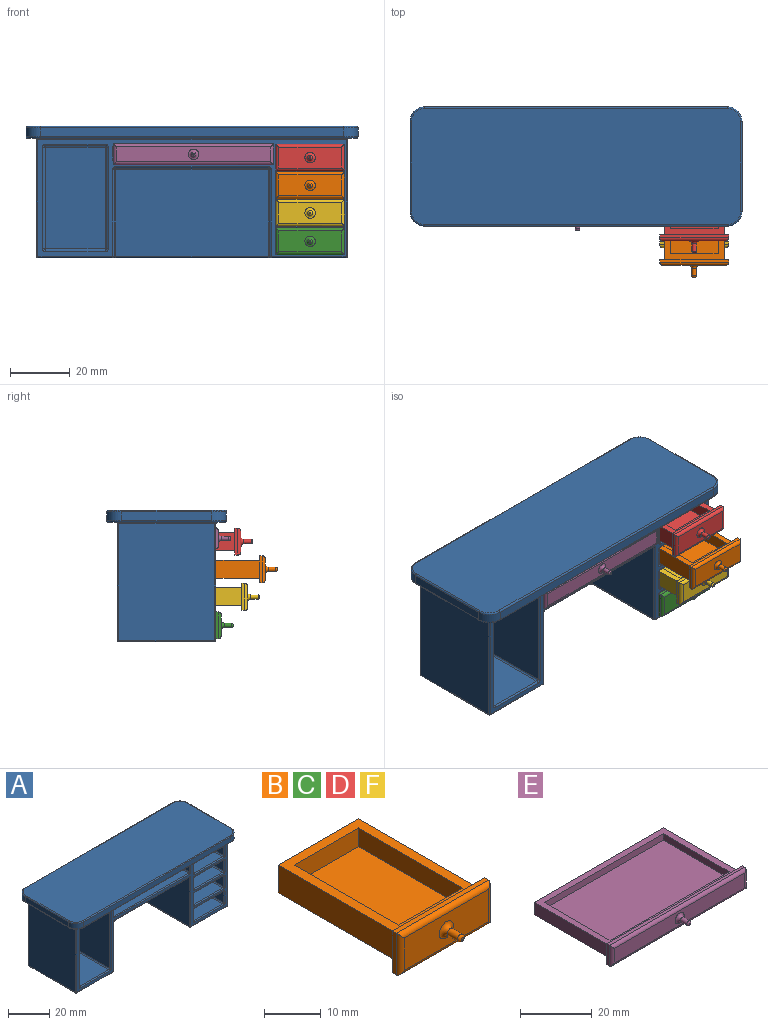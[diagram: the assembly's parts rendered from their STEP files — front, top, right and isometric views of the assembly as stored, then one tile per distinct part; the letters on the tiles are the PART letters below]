
ASSEMBLY  parts=6 mates=10
PART A: 225 faces, bbox 111.9x40.8x44 mm
  f0: plane 110.03x39mm, normal (0,0,-1), area 703.6mm2, adj f169,f170,f171,f173,f174,f175,f179,f180
  f1: plane 103.03x39mm, normal (0,-1,0), area 596.7mm2, adj f49,f50,f51,f52,f56,f57,f58,f61
  f2: plane 29x6.5mm, normal (-1,0,0), area 188.5mm2, adj f69,f72,f76,f77
  f3: plane 29x6.5mm, normal (1,0,0), area 188.5mm2, adj f74,f83,f84,f88
  f4: plane 20x6.25mm, normal (0,-1,0), area 125mm2, adj f54,f63,f64,f68
  f5: plane 29x6.25mm, normal (-1,0,0), area 181.2mm2, adj f57,f62,f65,f68
  f6: plane 29x6.25mm, normal (1,0,0), area 181.2mm2, adj f49,f53,f54,f55
  f7: plane 20x6.25mm, normal (0,-1,0), area 125mm2, adj f94,f103,f104,f108
  f8: plane 20x6mm, normal (0,-1,0), area 120mm2, adj f114,f123,f124,f128
  f9: plane 29x6.25mm, normal (-1,0,0), area 181.2mm2, adj f97,f102,f105,f108
  f10: plane 29x6.25mm, normal (1,0,0), area 181.2mm2, adj f89,f93,f94,f95
  f11: plane 29x29mm, normal (1,0,0), area 841mm2, adj f192,f193,f202,f203
  f12: plane 29x29mm, normal (-1,0,0), area 841mm2, adj f195,f196,f204,f205
  f13: plane 51.03x29mm, normal (0,0,-1), area 1479.8mm2, adj f184,f193,f194,f195
  f14: plane 30x3mm, normal (1,0,0), area 90mm2, adj f15,f21,f213,f221
  f15: cylinder r=5mm len=5mm, axis (0,0,1), area 23.6mm2, adj f14,f16,f211,f219
  f16: plane 101.03x3mm, normal (0,1,0), area 303.1mm2, adj f15,f17,f209,f217
  f17: cylinder r=5mm len=5mm, axis (0,0,1), area 23.6mm2, adj f16,f18,f210,f218
  f18: plane 30x3mm, normal (-1,0,0), area 90mm2, adj f17,f19,f212,f220
  f19: cylinder r=5mm len=5mm, axis (0,0,1), area 23.6mm2, adj f18,f20,f214,f222
  f20: plane 101.03x3mm, normal (0,-1,0), area 303.1mm2, adj f19,f21,f216,f224
  f21: cylinder r=5mm len=5mm, axis (0,0,1), area 23.6mm2, adj f14,f20,f215,f223
  f22: plane 110.03x39mm, normal (0,0,1), area 4273.7mm2, adj f209,f210,f211,f212,f213,f214,f215,f216
  f23: plane 39x32mm, normal (-1,0,0), area 1248mm2, adj f172,f173,f182,f183
  f24: plane 103.03x39mm, normal (0,1,0), area 4018.1mm2, adj f169,f172,f176,f177
  f25: plane 103.03x32mm, normal (0,0,-1), area 1706.5mm2, adj f177,f182,f186,f191,f197,f202,f205,f206
  f26: plane 39x32mm, normal (1,0,0), area 1248mm2, adj f175,f176,f185,f186
  f27: plane 51.03x29mm, normal (0,-1,0), area 1479.8mm2, adj f194,f203,f204,f208
  f28: plane 51.03x4mm, normal (0,-1,0), area 204.1mm2, adj f137,f142,f145,f148
  f29: plane 29x4mm, normal (1,0,0), area 116mm2, adj f135,f136,f144,f145
  f30: plane 51.03x29mm, normal (0,0,-1), area 1479.8mm2, adj f129,f132,f136,f137
  f31: plane 51.03x29mm, normal (0,0,1), area 1479.8mm2, adj f134,f143,f144,f148
  f32: plane 29x4mm, normal (-1,0,0), area 116mm2, adj f132,f133,f142,f143
  f33: plane 20x6.5mm, normal (0,-1,0), area 130mm2, adj f69,f73,f74,f75
  f34: plane 29x20mm, normal (0,0,-1), area 580mm2, adj f115,f116,f124,f125
  f35: plane 29x6mm, normal (-1,0,0), area 174mm2, adj f117,f122,f125,f128
  f36: plane 29x6mm, normal (1,0,0), area 174mm2, adj f109,f113,f114,f115
  f37: plane 29x20mm, normal (0,0,1), area 580mm2, adj f75,f76,f84,f85
  f38: plane 34x20mm, normal (0,-1,0), area 680mm2, adj f157,f162,f165,f168
  f39: plane 34x29mm, normal (1,0,0), area 986mm2, adj f155,f156,f164,f165
  f40: plane 29x20mm, normal (0,0,-1), area 580mm2, adj f149,f152,f156,f157
  f41: plane 29x20mm, normal (0,0,1), area 580mm2, adj f154,f163,f164,f168
  f42: plane 34x29mm, normal (-1,0,0), area 986mm2, adj f152,f153,f162,f163
  f43: plane 29x20mm, normal (0,0,-1), area 580mm2, adj f95,f96,f104,f105
  f44: plane 29x20mm, normal (0,0,1), area 580mm2, adj f112,f113,f122,f123
  f45: plane 29x20mm, normal (0,0,1), area 580mm2, adj f92,f93,f102,f103
  f46: plane 29x20mm, normal (0,0,-1), area 580mm2, adj f55,f56,f64,f65
  f47: plane 29x20mm, normal (0,0,1), area 580mm2, adj f52,f53,f62,f63
  f48: plane 29x20mm, normal (0,0,-1), area 580mm2, adj f72,f73,f82,f83
  f49: cylinder r=0.5mm len=6.25mm, axis (0,0,1), area 4.9mm2, adj f1,f6,f50,f51
  f50: torus R=1mm, axis (0,-1,0), area 0.8mm2, adj f1,f49,f52,f53
  f51: torus R=1mm, axis (0,-1,0), area 0.8mm2, adj f1,f49,f55,f56
  f52: cylinder r=0.5mm len=20mm, axis (1,0,0), area 15.7mm2, adj f1,f47,f50,f58
  f53: cylinder r=0.5mm len=29mm, axis (0,1,0), area 22.8mm2, adj f6,f47,f50,f59
  f54: cylinder r=0.5mm len=6.25mm, axis (0,0,1), area 4.9mm2, adj f4,f6,f59,f60
  f55: cylinder r=0.5mm len=29mm, axis (0,-1,0), area 22.8mm2, adj f6,f46,f51,f60
  f56: cylinder r=0.5mm len=20mm, axis (-1,0,0), area 15.7mm2, adj f1,f46,f51,f61
  f57: cylinder r=0.5mm len=6.25mm, axis (0,0,-1), area 4.9mm2, adj f1,f5,f58,f61
  f58: torus R=1mm, axis (0,-1,0), area 0.8mm2, adj f1,f52,f57,f62
  f59: sphere r=0.5mm, area 0.4mm2, adj f53,f54,f63
  f60: sphere r=0.5mm, area 0.4mm2, adj f54,f55,f64
  f61: torus R=1mm, axis (0,-1,0), area 0.8mm2, adj f1,f56,f57,f65
  f62: cylinder r=0.5mm len=29mm, axis (0,-1,0), area 22.8mm2, adj f5,f47,f58,f66
  f63: cylinder r=0.5mm len=20mm, axis (-1,0,0), area 15.7mm2, adj f4,f47,f59,f66
  f64: cylinder r=0.5mm len=20mm, axis (1,0,0), area 15.7mm2, adj f4,f46,f60,f67
  f65: cylinder r=0.5mm len=29mm, axis (0,1,0), area 22.8mm2, adj f5,f46,f61,f67
  f66: sphere r=0.5mm, area 0.4mm2, adj f62,f63,f68
  f67: sphere r=0.5mm, area 0.4mm2, adj f64,f65,f68
  f68: cylinder r=0.5mm len=6.25mm, axis (0,0,-1), area 4.9mm2, adj f4,f5,f66,f67
  f69: cylinder r=0.5mm len=6.5mm, axis (0,0,-1), area 5.1mm2, adj f2,f33,f70,f71
  f70: sphere r=0.5mm, area 0.4mm2, adj f69,f72,f73
  f71: sphere r=0.5mm, area 0.4mm2, adj f69,f75,f76
  f72: cylinder r=0.5mm len=29mm, axis (0,1,0), area 22.8mm2, adj f2,f48,f70,f78
  f73: cylinder r=0.5mm len=20mm, axis (1,0,0), area 15.7mm2, adj f33,f48,f70,f79
  f74: cylinder r=0.5mm len=6.5mm, axis (0,0,1), area 5.1mm2, adj f3,f33,f79,f80
  f75: cylinder r=0.5mm len=20mm, axis (-1,0,0), area 15.7mm2, adj f33,f37,f71,f80
  f76: cylinder r=0.5mm len=29mm, axis (0,1,0), area 22.8mm2, adj f2,f37,f71,f81
  f77: cylinder r=0.5mm len=6.5mm, axis (0,0,-1), area 5.1mm2, adj f1,f2,f78,f81
  f78: torus R=1mm, axis (0,-1,0), area 0.8mm2, adj f1,f72,f77,f82
  f79: sphere r=0.5mm, area 0.4mm2, adj f73,f74,f83
  f80: sphere r=0.5mm, area 0.4mm2, adj f74,f75,f84
  f81: torus R=1mm, axis (0,-1,0), area 0.8mm2, adj f1,f76,f77,f85
  f82: cylinder r=0.5mm len=20mm, axis (-1,0,0), area 15.7mm2, adj f1,f48,f78,f86
  f83: cylinder r=0.5mm len=29mm, axis (0,-1,0), area 22.8mm2, adj f3,f48,f79,f86
  f84: cylinder r=0.5mm len=29mm, axis (0,-1,0), area 22.8mm2, adj f3,f37,f80,f87
  f85: cylinder r=0.5mm len=20mm, axis (-1,0,0), area 15.7mm2, adj f1,f37,f81,f87
  f86: torus R=1mm, axis (0,-1,0), area 0.8mm2, adj f1,f82,f83,f88
  f87: torus R=1mm, axis (0,-1,0), area 0.8mm2, adj f1,f84,f85,f88
  f88: cylinder r=0.5mm len=6.5mm, axis (0,0,1), area 5.1mm2, adj f1,f3,f86,f87
  f89: cylinder r=0.5mm len=6.25mm, axis (0,0,1), area 4.9mm2, adj f1,f10,f90,f91
  f90: torus R=1mm, axis (0,-1,0), area 0.8mm2, adj f1,f89,f92,f93
  f91: torus R=1mm, axis (0,-1,0), area 0.8mm2, adj f1,f89,f95,f96
  f92: cylinder r=0.5mm len=20mm, axis (1,0,0), area 15.7mm2, adj f1,f45,f90,f98
  f93: cylinder r=0.5mm len=29mm, axis (0,1,0), area 22.8mm2, adj f10,f45,f90,f99
  f94: cylinder r=0.5mm len=6.25mm, axis (0,0,1), area 4.9mm2, adj f7,f10,f99,f100
  f95: cylinder r=0.5mm len=29mm, axis (0,-1,0), area 22.8mm2, adj f10,f43,f91,f100
  f96: cylinder r=0.5mm len=20mm, axis (-1,0,0), area 15.7mm2, adj f1,f43,f91,f101
  f97: cylinder r=0.5mm len=6.25mm, axis (0,0,-1), area 4.9mm2, adj f1,f9,f98,f101
  f98: torus R=1mm, axis (0,-1,0), area 0.8mm2, adj f1,f92,f97,f102
  f99: sphere r=0.5mm, area 0.4mm2, adj f93,f94,f103
  f100: sphere r=0.5mm, area 0.4mm2, adj f94,f95,f104
  f101: torus R=1mm, axis (0,-1,0), area 0.8mm2, adj f1,f96,f97,f105
  f102: cylinder r=0.5mm len=29mm, axis (0,-1,0), area 22.8mm2, adj f9,f45,f98,f106
  f103: cylinder r=0.5mm len=20mm, axis (-1,0,0), area 15.7mm2, adj f7,f45,f99,f106
  f104: cylinder r=0.5mm len=20mm, axis (1,0,0), area 15.7mm2, adj f7,f43,f100,f107
  f105: cylinder r=0.5mm len=29mm, axis (0,1,0), area 22.8mm2, adj f9,f43,f101,f107
  f106: sphere r=0.5mm, area 0.4mm2, adj f102,f103,f108
  f107: sphere r=0.5mm, area 0.4mm2, adj f104,f105,f108
  f108: cylinder r=0.5mm len=6.25mm, axis (0,0,-1), area 4.9mm2, adj f7,f9,f106,f107
  f109: cylinder r=0.5mm len=6mm, axis (0,0,1), area 4.7mm2, adj f1,f36,f110,f111
  f110: torus R=1mm, axis (0,-1,0), area 0.8mm2, adj f1,f109,f112,f113
  f111: torus R=1mm, axis (0,-1,0), area 0.8mm2, adj f1,f109,f115,f116
  f112: cylinder r=0.5mm len=20mm, axis (1,0,0), area 15.7mm2, adj f1,f44,f110,f118
  f113: cylinder r=0.5mm len=29mm, axis (0,1,0), area 22.8mm2, adj f36,f44,f110,f119
  f114: cylinder r=0.5mm len=6mm, axis (0,0,1), area 4.7mm2, adj f8,f36,f119,f120
  f115: cylinder r=0.5mm len=29mm, axis (0,1,0), area 22.8mm2, adj f34,f36,f111,f120
  f116: cylinder r=0.5mm len=20mm, axis (1,0,0), area 15.7mm2, adj f1,f34,f111,f121
  f117: cylinder r=0.5mm len=6mm, axis (0,0,-1), area 4.7mm2, adj f1,f35,f118,f121
  f118: torus R=1mm, axis (0,-1,0), area 0.8mm2, adj f1,f112,f117,f122
  f119: sphere r=0.5mm, area 0.4mm2, adj f113,f114,f123
  f120: sphere r=0.5mm, area 0.4mm2, adj f114,f115,f124
  f121: torus R=1mm, axis (0,-1,0), area 0.8mm2, adj f1,f116,f117,f125
  f122: cylinder r=0.5mm len=29mm, axis (0,-1,0), area 22.8mm2, adj f35,f44,f118,f126
  f123: cylinder r=0.5mm len=20mm, axis (-1,0,0), area 15.7mm2, adj f8,f44,f119,f126
  f124: cylinder r=0.5mm len=20mm, axis (1,0,0), area 15.7mm2, adj f8,f34,f120,f127
  f125: cylinder r=0.5mm len=29mm, axis (0,-1,0), area 22.8mm2, adj f34,f35,f121,f127
  f126: sphere r=0.5mm, area 0.4mm2, adj f122,f123,f128
  f127: sphere r=0.5mm, area 0.4mm2, adj f124,f125,f128
  f128: cylinder r=0.5mm len=6mm, axis (0,0,-1), area 4.7mm2, adj f8,f35,f126,f127
  f129: cylinder r=0.5mm len=51.03mm, axis (1,0,0), area 40.1mm2, adj f1,f30,f130,f131
  f130: torus R=1mm, axis (0,-1,0), area 0.8mm2, adj f1,f129,f132,f133
  f131: torus R=1mm, axis (0,-1,0), area 0.8mm2, adj f1,f129,f135,f136
  f132: cylinder r=0.5mm len=29mm, axis (0,1,0), area 22.8mm2, adj f30,f32,f130,f138
  f133: cylinder r=0.5mm len=4mm, axis (0,0,-1), area 3.1mm2, adj f1,f32,f130,f139
  f134: cylinder r=0.5mm len=51.03mm, axis (-1,0,0), area 40.1mm2, adj f1,f31,f139,f140
  f135: cylinder r=0.5mm len=4mm, axis (0,0,1), area 3.1mm2, adj f1,f29,f131,f140
  f136: cylinder r=0.5mm len=29mm, axis (0,-1,0), area 22.8mm2, adj f29,f30,f131,f141
  f137: cylinder r=0.5mm len=51.03mm, axis (1,0,0), area 40.1mm2, adj f28,f30,f138,f141
  f138: sphere r=0.5mm, area 0.4mm2, adj f132,f137,f142
  f139: torus R=1mm, axis (0,-1,0), area 0.8mm2, adj f1,f133,f134,f143
  f140: torus R=1mm, axis (0,-1,0), area 0.8mm2, adj f1,f134,f135,f144
  f141: sphere r=0.5mm, area 0.4mm2, adj f136,f137,f145
  f142: cylinder r=0.5mm len=4mm, axis (0,0,-1), area 3.1mm2, adj f28,f32,f138,f146
  f143: cylinder r=0.5mm len=29mm, axis (0,-1,0), area 22.8mm2, adj f31,f32,f139,f146
  f144: cylinder r=0.5mm len=29mm, axis (0,1,0), area 22.8mm2, adj f29,f31,f140,f147
  f145: cylinder r=0.5mm len=4mm, axis (0,0,1), area 3.1mm2, adj f28,f29,f141,f147
  f146: sphere r=0.5mm, area 0.4mm2, adj f142,f143,f148
  f147: sphere r=0.5mm, area 0.4mm2, adj f144,f145,f148
  f148: cylinder r=0.5mm len=51.03mm, axis (-1,0,0), area 40.1mm2, adj f28,f31,f146,f147
  f149: cylinder r=0.5mm len=20mm, axis (1,0,0), area 15.7mm2, adj f1,f40,f150,f151
  f150: torus R=1mm, axis (0,-1,0), area 0.8mm2, adj f1,f149,f152,f153
  f151: torus R=1mm, axis (0,-1,0), area 0.8mm2, adj f1,f149,f155,f156
  f152: cylinder r=0.5mm len=29mm, axis (0,1,0), area 22.8mm2, adj f40,f42,f150,f158
  f153: cylinder r=0.5mm len=34mm, axis (0,0,-1), area 26.7mm2, adj f1,f42,f150,f159
  f154: cylinder r=0.5mm len=20mm, axis (-1,0,0), area 15.7mm2, adj f1,f41,f159,f160
  f155: cylinder r=0.5mm len=34mm, axis (0,0,1), area 26.7mm2, adj f1,f39,f151,f160
  f156: cylinder r=0.5mm len=29mm, axis (0,-1,0), area 22.8mm2, adj f39,f40,f151,f161
  f157: cylinder r=0.5mm len=20mm, axis (1,0,0), area 15.7mm2, adj f38,f40,f158,f161
  f158: sphere r=0.5mm, area 0.4mm2, adj f152,f157,f162
  f159: torus R=1mm, axis (0,-1,0), area 0.8mm2, adj f1,f153,f154,f163
  f160: torus R=1mm, axis (0,-1,0), area 0.8mm2, adj f1,f154,f155,f164
  f161: sphere r=0.5mm, area 0.4mm2, adj f156,f157,f165
  f162: cylinder r=0.5mm len=34mm, axis (0,0,-1), area 26.7mm2, adj f38,f42,f158,f166
  f163: cylinder r=0.5mm len=29mm, axis (0,-1,0), area 22.8mm2, adj f41,f42,f159,f166
  f164: cylinder r=0.5mm len=29mm, axis (0,1,0), area 22.8mm2, adj f39,f41,f160,f167
  f165: cylinder r=0.5mm len=34mm, axis (0,0,1), area 26.7mm2, adj f38,f39,f161,f167
  f166: sphere r=0.5mm, area 0.4mm2, adj f162,f163,f168
  f167: sphere r=0.5mm, area 0.4mm2, adj f164,f165,f168
  f168: cylinder r=0.5mm len=20mm, axis (-1,0,0), area 15.7mm2, adj f38,f41,f166,f167
  f169: cylinder r=0.5mm len=103.03mm, axis (-1,0,0), area 80.9mm2, adj f0,f24,f170,f171
  f170: torus R=1mm, axis (0,0,1), area 0.8mm2, adj f0,f169,f172,f173
  f171: torus R=1mm, axis (0,0,1), area 0.8mm2, adj f0,f169,f175,f176
  f172: cylinder r=0.5mm len=39mm, axis (0,0,1), area 30.6mm2, adj f23,f24,f170,f178
  f173: cylinder r=0.5mm len=32mm, axis (0,-1,0), area 25.1mm2, adj f0,f23,f170,f179
  f174: cylinder r=0.5mm len=103.03mm, axis (1,0,0), area 80.9mm2, adj f0,f1,f179,f180
  f175: cylinder r=0.5mm len=32mm, axis (0,1,0), area 25.1mm2, adj f0,f26,f171,f180
  f176: cylinder r=0.5mm len=39mm, axis (0,0,-1), area 30.6mm2, adj f24,f26,f171,f181
  f177: cylinder r=0.5mm len=103.03mm, axis (-1,0,0), area 80.9mm2, adj f24,f25,f178,f181
  f178: sphere r=0.5mm, area 0.4mm2, adj f172,f177,f182
  f179: torus R=1mm, axis (0,0,1), area 0.8mm2, adj f0,f173,f174,f183
  f180: torus R=1mm, axis (0,0,1), area 0.8mm2, adj f0,f174,f175,f185
  f181: sphere r=0.5mm, area 0.4mm2, adj f176,f177,f186
  f182: cylinder r=0.5mm len=32mm, axis (0,-1,0), area 25.1mm2, adj f23,f25,f178,f187
  f183: cylinder r=0.5mm len=39mm, axis (0,0,-1), area 30.6mm2, adj f1,f23,f179,f187
  f184: cylinder r=0.5mm len=51.03mm, axis (1,0,0), area 40.1mm2, adj f1,f13,f188,f189
  f185: cylinder r=0.5mm len=39mm, axis (0,0,1), area 30.6mm2, adj f1,f26,f180,f190
  f186: cylinder r=0.5mm len=32mm, axis (0,1,0), area 25.1mm2, adj f25,f26,f181,f190
  f187: sphere r=0.5mm, area 0.4mm2, adj f182,f183,f191
  f188: torus R=1mm, axis (0,-1,0), area 0.8mm2, adj f1,f184,f192,f193
  f189: torus R=1mm, axis (0,-1,0), area 0.8mm2, adj f1,f184,f195,f196
  f190: sphere r=0.5mm, area 0.4mm2, adj f185,f186,f197
  f191: cylinder r=0.5mm len=25mm, axis (1,0,0), area 19.6mm2, adj f1,f25,f187,f198
  f192: cylinder r=0.5mm len=29mm, axis (0,0,1), area 22.8mm2, adj f1,f11,f188,f198
  f193: cylinder r=0.5mm len=29mm, axis (0,-1,0), area 22.8mm2, adj f11,f13,f188,f199
  f194: cylinder r=0.5mm len=51.03mm, axis (-1,0,0), area 40.1mm2, adj f13,f27,f199,f200
  f195: cylinder r=0.5mm len=29mm, axis (0,1,0), area 22.8mm2, adj f12,f13,f189,f200
  f196: cylinder r=0.5mm len=29mm, axis (0,0,-1), area 22.8mm2, adj f1,f12,f189,f201
  f197: cylinder r=0.5mm len=25mm, axis (-1,0,0), area 19.6mm2, adj f1,f25,f190,f201
  f198: sphere r=0.5mm, area 0.4mm2, adj f191,f192,f202
  f199: sphere r=0.5mm, area 0.4mm2, adj f193,f194,f203
  f200: sphere r=0.5mm, area 0.4mm2, adj f194,f195,f204
  f201: sphere r=0.5mm, area 0.4mm2, adj f196,f197,f205
  f202: cylinder r=0.5mm len=29mm, axis (0,1,0), area 22.8mm2, adj f11,f25,f198,f206
  f203: cylinder r=0.5mm len=29mm, axis (0,0,-1), area 22.8mm2, adj f11,f27,f199,f206
  f204: cylinder r=0.5mm len=29mm, axis (0,0,1), area 22.8mm2, adj f12,f27,f200,f207
  f205: cylinder r=0.5mm len=29mm, axis (0,-1,0), area 22.8mm2, adj f12,f25,f201,f207
  f206: torus R=1mm, axis (0,0,-1), area 0.8mm2, adj f25,f202,f203,f208
  f207: torus R=1mm, axis (0,0,-1), area 0.8mm2, adj f25,f204,f205,f208
  f208: cylinder r=0.5mm len=51.03mm, axis (1,0,0), area 40.1mm2, adj f25,f27,f206,f207
  f209: cylinder r=0.5mm len=101.03mm, axis (-1,0,0), area 79.3mm2, adj f16,f22,f210,f211
  f210: torus R=4.5mm, axis (0,0,1), area 5.9mm2, adj f17,f22,f209,f212
  f211: torus R=4.5mm, axis (0,0,1), area 5.9mm2, adj f15,f22,f209,f213
  f212: cylinder r=0.5mm len=30mm, axis (0,-1,0), area 23.6mm2, adj f18,f22,f210,f214
  f213: cylinder r=0.5mm len=30mm, axis (0,1,0), area 23.6mm2, adj f14,f22,f211,f215
  f214: torus R=4.5mm, axis (0,0,1), area 5.9mm2, adj f19,f22,f212,f216
  f215: torus R=4.5mm, axis (0,0,1), area 5.9mm2, adj f21,f22,f213,f216
  f216: cylinder r=0.5mm len=101.03mm, axis (1,0,0), area 79.3mm2, adj f20,f22,f214,f215
  f217: cylinder r=0.5mm len=101.03mm, axis (1,0,0), area 79.3mm2, adj f0,f16,f218,f219
  f218: torus R=4.5mm, axis (0,0,1), area 5.9mm2, adj f0,f17,f217,f220
  f219: torus R=4.5mm, axis (0,0,1), area 5.9mm2, adj f0,f15,f217,f221
  f220: cylinder r=0.5mm len=30mm, axis (0,1,0), area 23.6mm2, adj f0,f18,f218,f222
  f221: cylinder r=0.5mm len=30mm, axis (0,-1,0), area 23.6mm2, adj f0,f14,f219,f223
  f222: torus R=4.5mm, axis (0,0,1), area 5.9mm2, adj f0,f19,f220,f224
  f223: torus R=4.5mm, axis (0,0,1), area 5.9mm2, adj f0,f21,f221,f224
  f224: cylinder r=0.5mm len=101.03mm, axis (-1,0,0), area 79.3mm2, adj f0,f20,f222,f223
PART B: 24 faces, bbox 23x36x9 mm
  f0: plane 30x20mm, normal (0,0,1), area 184mm2, adj f1,f3,f4,f5,f7,f8,f9,f15
  f1: plane 30x6mm, normal (-1,0,0), area 180mm2, adj f0,f2,f4,f15
  f2: plane 30x20mm, normal (0,0,-1), area 600mm2, adj f1,f3,f4,f15
  f3: plane 30x6mm, normal (1,0,0), area 180mm2, adj f0,f2,f4,f15
  f4: plane 20x6mm, normal (0,1,0), area 120mm2, adj f0,f1,f2,f3
  f5: plane 26x4mm, normal (1,0,0), area 104mm2, adj f0,f6,f8,f9
  f6: plane 26x16mm, normal (0,0,1), area 416mm2, adj f5,f7,f8,f9
  f7: plane 26x4mm, normal (-1,0,0), area 104mm2, adj f0,f6,f8,f9
  f8: plane 16x4mm, normal (0,1,0), area 64mm2, adj f0,f5,f6,f7
  f9: plane 16x4mm, normal (0,-1,0), area 64mm2, adj f0,f5,f6,f7
  f10: plane 23x1mm, normal (0,0,1), area 23mm2, adj f11,f13,f15,f20
  f11: plane 9x1mm, normal (-1,0,0), area 9mm2, adj f10,f12,f15,f21
  f12: plane 23x1mm, normal (0,0,-1), area 23mm2, adj f11,f13,f15,f23
  f13: plane 9x1mm, normal (1,0,0), area 9mm2, adj f10,f12,f15,f22
  f14: plane 21x7mm, normal (0,-1,0), area 137.4mm2, adj f19,f20,f21,f22,f23
  f15: plane 23x9mm, normal (0,1,0), area 87mm2, adj f0,f1,f2,f3,f10,f11,f12,f13
  f16: cylinder r=0.75mm len=2.5mm, axis (0,1,0), area 11.8mm2, adj f18,f19
  f17: plane 0.5x0.5mm, normal (0,-1,0), area 0.2mm2, adj f18
  f18: torus R=0.25mm, axis (0,-1,0), area 2.8mm2, adj f16,f17
  f19: torus R=1.75mm, axis (0,-1,0), area 11mm2, adj f14,f16
  f20: cylinder r=1mm len=23mm, axis (1,0,0), area 35mm2, adj f10,f14,f21,f22
  f21: cylinder r=1mm len=9mm, axis (0,0,1), area 13mm2, adj f11,f14,f20,f23
  f22: cylinder r=1mm len=9mm, axis (0,0,-1), area 13mm2, adj f13,f14,f20,f23
  f23: cylinder r=1mm len=23mm, axis (-1,0,0), area 35mm2, adj f12,f14,f21,f22
PART C: same geometry as B
PART D: same geometry as B
PART E: 24 faces, bbox 53.5x36x7 mm
  f0: plane 51x30mm, normal (0,0,1), area 308mm2, adj f1,f3,f4,f5,f7,f8,f9,f15
  f1: plane 30x4.2mm, normal (-1,0,0), area 126mm2, adj f0,f2,f4,f15
  f2: plane 51x30mm, normal (0,0,-1), area 1530mm2, adj f1,f3,f4,f15
  f3: plane 30x4.2mm, normal (1,0,0), area 126mm2, adj f0,f2,f4,f15
  f4: plane 51x4.2mm, normal (0,1,0), area 214.2mm2, adj f0,f1,f2,f3
  f5: plane 26x2.2mm, normal (1,0,0), area 57.2mm2, adj f0,f6,f8,f9
  f6: plane 47x26mm, normal (0,0,1), area 1222mm2, adj f5,f7,f8,f9
  f7: plane 26x2.2mm, normal (-1,0,0), area 57.2mm2, adj f0,f6,f8,f9
  f8: plane 47x2.2mm, normal (0,1,0), area 103.4mm2, adj f0,f5,f6,f7
  f9: plane 47x2.2mm, normal (0,-1,0), area 103.4mm2, adj f0,f5,f6,f7
  f10: plane 53.53x1mm, normal (0,0,1), area 53.5mm2, adj f11,f13,f15,f20
  f11: plane 7x1mm, normal (-1,0,0), area 7mm2, adj f10,f12,f15,f21
  f12: plane 53.53x1mm, normal (0,0,-1), area 53.5mm2, adj f11,f13,f15,f23
  f13: plane 7x1mm, normal (1,0,0), area 7mm2, adj f10,f12,f15,f22
  f14: plane 51.53x5mm, normal (0,-1,0), area 248mm2, adj f19,f20,f21,f22,f23
  f15: plane 53.53x7mm, normal (0,1,0), area 160.5mm2, adj f0,f1,f2,f3,f10,f11,f12,f13
  f16: cylinder r=0.75mm len=2.5mm, axis (0,1,0), area 11.8mm2, adj f18,f19
  f17: plane 0.5x0.5mm, normal (0,-1,0), area 0.2mm2, adj f18
  f18: torus R=0.25mm, axis (0,-1,0), area 2.8mm2, adj f16,f17
  f19: torus R=1.75mm, axis (0,-1,0), area 11mm2, adj f14,f16
  f20: cylinder r=1mm len=53.53mm, axis (1,0,0), area 82.9mm2, adj f10,f14,f21,f22
  f21: cylinder r=1mm len=7mm, axis (0,0,1), area 9.9mm2, adj f11,f14,f20,f23
  f22: cylinder r=1mm len=7mm, axis (0,0,-1), area 9.9mm2, adj f13,f14,f20,f23
  f23: cylinder r=1mm len=53.53mm, axis (-1,0,0), area 82.9mm2, adj f12,f14,f21,f22
PART F: same geometry as B
PLACE A t=(-24.88,3.76,-3.6)mm fixed
PLACE B t=(14.63,2.76,-23.35)mm
PLACE C t=(14.63,17.51,-42.1)mm
PLACE D t=(14.63,10.91,-14.1)mm
PLACE E t=(-24.37,18.42,-13)mm
PLACE F t=(14.63,8.64,-32.6)mm
MATE planar B.f2 <-> A.f45  axis (0,0,-1) through (14.63,-12.24,-26.35)mm
MATE planar C.f2 <-> A.f37  axis (0,0,-1) through (14.63,2.51,-45.1)mm
MATE planar B.f3 <-> A.f9  axis (1,0,0) through (24.63,-12.24,-23.35)mm
MATE planar F.f3 <-> A.f5  axis (1,0,0) through (24.63,-6.36,-32.6)mm
MATE planar F.f2 <-> A.f47  axis (0,0,-1) through (14.63,-6.36,-35.6)mm
MATE planar D.f2 <-> A.f44  axis (0,0,-1) through (14.63,-4.09,-17.1)mm
MATE planar D.f3 <-> A.f35  axis (1,0,0) through (24.63,-4.09,-14.1)mm
MATE planar E.f3 <-> A.f32  axis (1,0,0) through (1.13,3.42,-13)mm
MATE planar E.f2 <-> A.f31  axis (0,0,-1) through (-24.37,3.42,-15.1)mm
MATE planar C.f3 <-> A.f2  axis (1,0,0) through (24.63,2.51,-42.1)mm
